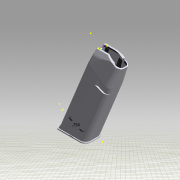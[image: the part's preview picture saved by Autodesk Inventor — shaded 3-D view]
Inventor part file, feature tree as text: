
AUTODESK INVENTOR PART (.ipt)
format: ipt  version: 2018 (Build 220112000, 112)  size: 5,122,560 bytes
history: native  units: mm (DEFAULTED — no unit token found)
features: sketch x117, extrude x106, projected_geometry x105, mirror x43, plane x19, fillet x14, direct_edit x5, other x5, chamfer x4, loft x2, revolve x2, sweep x1
ambient origin geometry x8: Origin, YZ Plane, XZ Plane, XY Plane, X Axis, Y Axis, Z Axis, Center Point
bodies: Solid2 (feature_tree), Solid1 (feature_tree)
feature tree (423):
  direct_edit  "Direct Edit1"
  direct_edit  "Direct Edit2"
  direct_edit  "Direct Edit3"
  extrude  "Extrusion1"  Depth=10.0mm
  extrude  "Extrusion2"  Depth=0.4064mm
  extrude  "Extrusion3"  Depth=25.4mm TaperAngle=0.0deg
  extrude  "Extrusion4"  Depth=0.4064mm TaperAngle=0.0deg
  fillet  "Fillet1"  Radius=0.254mm
  extrude  "Extrusion5"  Depth=1.905mm
  extrude  "Extrusion7"  Depth=50.8mm TaperAngle=0.0deg
  extrude  "Extrusion8"  Depth=2.54mm TaperAngle=0.0deg
  extrude  "Extrusion9"  Depth=2.54mm TaperAngle=0.0deg
  extrude  "Extrusion10"  [1 undecoded]
  extrude  "Extrusion11"  Depth=4.0mm TaperAngle=0.0deg
  extrude  "Extrusion12"  Depth=4.0mm TaperAngle=0.0deg
  extrude  "Extrusion13"  Depth=8.0mm TaperAngle=0.0deg
  direct_edit  "Direct Edit4"
  plane  "Work Plane1"
  plane  "Work Plane2"
  extrude  "Extrusion20"  Depth=2.0mm TaperAngle=0.0deg
  extrude  "Extrusion21"  Depth=2.0mm TaperAngle=0.0deg
  mirror  "Mirror2"
  extrude  "Extrusion22"  [1 undecoded]
  extrude  "Extrusion23"  Depth=2.0mm TaperAngle=0.0deg
  extrude  "Extrusion24"  Depth=2.0mm TaperAngle=0.0deg
  mirror  "Mirror3"
  extrude  "Extrusion25"  Depth=2.0mm TaperAngle=0.0deg
  extrude  "Extrusion26"  Depth=2.0mm TaperAngle=0.0deg
  extrude  "Extrusion27"  Depth=2.0mm TaperAngle=0.0deg
  extrude  "Extrusion28"  Depth=2.0mm TaperAngle=0.0deg
  extrude  "Extrusion29"  TaperAngle=0.0deg  [1 undecoded]
  extrude  "Extrusion30"  Depth=0.5mm TaperAngle=0.0deg
  plane  "Work Plane3"
  extrude  "Extrusion31"  Depth=0.142mm TaperAngle=0.0deg
  extrude  "Extrusion32"  Depth=0.142mm TaperAngle=0.0deg
  extrude  "Extrusion33"  Depth=0.142mm TaperAngle=0.0deg
  mirror  "Mirror4"
  extrude  "Extrusion34"  Depth=0.142mm TaperAngle=0.0deg
  extrude  "Extrusion36"  Depth=4.3053mm
  extrude  "Extrusion37"  Depth=1.0mm TaperAngle=0.0deg
  extrude  "Extrusion38"  TaperAngle=0.0deg  [1 undecoded]
  extrude  "Extrusion39"  Depth=0.05mm TaperAngle=0.0deg
  mirror  "Mirror5"
  extrude  "Extrusion41"  Depth=25.4mm TaperAngle=0.0deg
  extrude  "Extrusion42"  Depth=25.4mm TaperAngle=0.0deg
  extrude  "Extrusion43"  Depth=304.8mm TaperAngle=0.0deg
  mirror  "Mirror6"
  mirror  "Mirror7"
  extrude  "Extrusion44"  Depth=2.54mm
  loft  "Loft1"
  mirror  "Mirror8"
  sketch  "Sketch62"  dims[d190=12.7mm d191=0.0mm d237=90.0deg]
  sketch  "Sketch63"  dims[d238=0.2032mm d240=2.54mm]
  sketch  "Sketch64"  dims[d241=0.0mm d242=0.0mm d245=1.27mm d246=0.0mm]
  plane  "Work Plane5"
  extrude  "Extrusion45"  Depth=12.7mm TaperAngle=0.0deg
  extrude  "Extrusion46"  TaperAngle=90.0deg  [1 undecoded]
  extrude  "Extrusion47"  Depth=2.54mm
  extrude  "Extrusion48"  Depth=1.27mm TaperAngle=0.0deg
  extrude  "Extrusion49"  Depth=0.381mm
  extrude  "Extrusion50"  Depth=0.1905mm
  extrude  "Extrusion51"  Depth=0.254mm TaperAngle=0.0deg
  extrude  "Extrusion52"  Depth=0.254mm TaperAngle=0.0deg
  extrude  "Extrusion54"  Depth=0.254mm
  extrude  "Extrusion55"  Depth=0.35mm TaperAngle=0.0deg
  extrude  "Extrusion56"  TaperAngle=90.0deg  [1 undecoded]
  mirror  "Mirror9"
  extrude  "Extrusion57"  Depth=2.413mm TaperAngle=0.0deg
  plane  "Work Plane6"
  loft  "Loft2"
  mirror  "Mirror10"
  mirror  "Mirror11"
  extrude  "Extrusion58"  Depth=2.794mm
  direct_edit  "Direct Edit6"
  extrude  "Extrusion60"  Depth=381.0mm
  mirror  "Mirror14"
  plane  "Work Plane7"
  extrude  "Extrusion61"  Depth=762.0mm
  mirror  "Mirror15"
  plane  "Work Plane8"
  extrude  "Extrusion62"  Depth=0.635mm
  mirror  "Mirror16"
  extrude  "Extrusion63"  Depth=96.52mm TaperAngle=0.0deg
  fillet  "Fillet3"  Radius=254.0mm
  extrude  "Extrusion65"  Depth=0.635mm
  mirror  "Mirror18"
  plane  "Work Plane9"
  extrude  "Extrusion66"  Depth=83.82mm TaperAngle=0.0deg
  extrude  "Extrusion67"  TaperAngle=90.0deg  [1 undecoded]
  mirror  "Mirror19"
  plane  "Work Plane16"
  plane  "Work Plane15"
  fillet  "Fillet20"  Radius=0.762mm
  sweep  "Sweep3"
  plane  "Work Plane17"
  extrude  "Extrusion81"  Depth=25.4mm TaperAngle=0.0deg
  extrude  "Extrusion82"  Depth=25.4mm TaperAngle=0.0deg
  mirror  "Mirror30"
  sketch  "Sketch133"  dims[d363=25.4mm d364=0.0mm d410=1.016mm d411=0.0mm]
  extrude  "Extrusion84"  Depth=0.381mm TaperAngle=0.0deg
  mirror  "Mirror32"
  extrude  "Extrusion85"  Depth=1.016mm TaperAngle=0.0deg
  extrude  "Extrusion86"  Depth=1.016mm TaperAngle=0.0deg
  extrude  "Extrusion87"  Depth=1.778mm TaperAngle=0.0deg
  fillet  "Fillet21"  Radius=1.27mm
  mirror  "Mirror33"
  mirror  "Mirror34"
  extrude  "Extrusion88"  Depth=88.9mm TaperAngle=0.0deg
  mirror  "Mirror35"
  extrude  "Extrusion89"  Depth=1.27mm TaperAngle=0.0deg
  chamfer  "Chamfer1"  Distance=3.048mm
  plane  "Work Plane18"
  extrude  "Extrusion90"  Depth=2.54mm TaperAngle=0.0deg
  extrude  "Extrusion91"  Depth=19.15mm
  mirror  "Mirror36"
  plane  "Work Plane19"
  extrude  "Extrusion92"  Depth=2.54mm TaperAngle=0.0deg
  chamfer  "Chamfer2"  Distance=2.54mm
  chamfer  "Chamfer3"  Distance=2.54mm
  extrude  "Extrusion93"  Depth=2.54mm TaperAngle=0.0deg
  mirror  "Mirror37"
  fillet  "Fillet23"  Radius=0.5588mm
  chamfer  "Chamfer4"  Distance=25.4mm
  fillet  "Fillet24"  Radius=25.4mm
  fillet  "Fillet25"  Radius=25.4mm
  fillet  "Fillet26"  Radius=25.4mm
  mirror  "Mirror39"
  extrude  "Extrusion94"  Depth=2.032mm TaperAngle=0.0deg
  mirror  "Mirror40"
  fillet  "Fillet27"  Radius=1.524mm
  extrude  "Extrusion95"  Depth=0.381mm TaperAngle=0.0deg
  mirror  "Mirror41"
  extrude  "Extrusion96"  Depth=0.5588mm
  mirror  "Mirror42"
  plane  "Work Plane20"
  plane  "Work Plane21"
  plane  "Work Plane22"
  extrude  "Extrusion97"  Depth=0.254mm
  mirror  "Mirror43"
  extrude  "Extrusion98"  [1 undecoded]
  extrude  "Extrusion99"  [1 undecoded]
  extrude  "Extrusion100"  [1 undecoded]
  extrude  "Extrusion101"  [1 undecoded]
  extrude  "Extrusion102"  [1 undecoded]
  mirror  "Mirror44"
  extrude  "Extrusion104"  [1 undecoded]
  extrude  "Extrusion105"  [1 undecoded]
  mirror  "Mirror46"
  extrude  "Extrusion106"  [1 undecoded]
  mirror  "Mirror47"
  plane  "Work Plane23"
  extrude  "Extrusion127"  [1 undecoded]
  extrude  "Extrusion128"  [1 undecoded]
  extrude  "Extrusion129"  [1 undecoded]
  extrude  "Extrusion130"  [1 undecoded]
  mirror  "Mirror50"
  sketch  "Sketch192"
  extrude  "Extrusion132"  [1 undecoded]
  extrude  "Extrusion133"  [1 undecoded]
  mirror  "Mirror52"
  extrude  "Extrusion134"  [1 undecoded]
  mirror  "Mirror53"
  extrude  "Extrusion135"  [1 undecoded]
  extrude  "Extrusion136"  [1 undecoded]
  extrude  "Extrusion137"  [1 undecoded]
  mirror  "Mirror54"
  extrude  "Extrusion138"  [1 undecoded]
  extrude  "Extrusion139"  [1 undecoded]
  extrude  "Extrusion140"  [1 undecoded]
  extrude  "Extrusion141"  [1 undecoded]
  sketch  "Sketch202"
  mirror  "Mirror55"
  sketch  "Sketch203"
  sketch  "Sketch204"
  sketch  "Sketch205"
  extrude  "Extrusion143"  [1 undecoded]
  mirror  "Mirror56"
  extrude  "Extrusion144"  [1 undecoded]
  extrude  "Extrusion146"  [1 undecoded]
  mirror  "Mirror58"
  extrude  "Extrusion147"  [1 undecoded]
  mirror  "Mirror59"
  fillet  "Fillet38"  [1 undecoded]
  extrude  "Extrusion148"  [1 undecoded]
  extrude  "Extrusion150"  [1 undecoded]
  mirror  "Mirror60"
  plane  "Work Plane24"
  sketch  "Sketch216"
  extrude  "Extrusion153"  [1 undecoded]
  mirror  "Mirror61"
  sketch  "Sketch217"
  extrude  "Extrusion154"  [1 undecoded]
  extrude  "Extrusion155"  [1 undecoded]
  sketch  "Sketch224"
  extrude  "Extrusion156"  [1 undecoded]
  fillet  "Fillet39"  [1 undecoded]
  fillet  "Fillet40"  [1 undecoded]
  sketch  "Sketch226"
  sketch  "Sketch227"
  sketch  "Sketch228"
  extrude  "Extrusion158"  [1 undecoded]
  extrude  "Extrusion159"  [1 undecoded]
  mirror  "Mirror64"
  fillet  "Fillet44"  [1 undecoded]
  extrude  "Extrusion160"  [1 undecoded]
  fillet  "Fillet45"  [1 undecoded]
  mirror  "Mirror65"
  mirror  "Mirror66"
  sketch  "Sketch1"  dims[d0=9.75mm d1=10.0mm d2=10.0mm d3=10.0mm d4=10.0mm d5=10.15mm]
  projected_geometry  "Projected Loop1"
  projected_geometry  "Projected Loop2"
  projected_geometry  "Projected Loop3"
  sketch  "Sketch4"  dims[d6=10.0mm d7=10.3mm d8=10.0mm d9=0.4064mm]
  projected_geometry  "Projected Loop4"
  projected_geometry  "Projected Loop5"
  sketch  "Sketch5"  dims[d10=25.4mm d11=0.0mm d12=25.4mm d13=0.0mm]
  projected_geometry  "Projected Loop6"
  sketch  "Sketch6"  dims[d14=2.54mm d15=0.0mm d16=0.4064mm d17=0.0mm d18=0.254mm]
  projected_geometry  "Projected Loop7"
  sketch  "Sketch9"  dims[d19=50.8mm d20=0.0mm d21=1.905mm]
  sketch  "Sketch10"  dims[d24=50.8mm d25=0.0mm d26=50.8mm d27=0.0mm]
  sketch  "Sketch11"  dims[d28=2.54mm d29=0.0mm d30=2.54mm d31=0.0mm]
  projected_geometry  "Projected Loop8"
  sketch  "Sketch12"  dims[d32=2.54mm d33=0.0mm d34=2.54mm d35=0.0mm]
  projected_geometry  "Projected Loop9"
  sketch  "Sketch13"  dims[d36=1.0mm d37=0.0mm d39=-3.665191mm]
  projected_geometry  "Projected Loop10"
  sketch  "Sketch14"  dims[d57=1.5mm d58=0.0mm d59=4.0mm d60=0.0mm]
  sketch  "Sketch15"  dims[d61=4.0mm d62=0.0mm d63=4.0mm d64=0.0mm]
  projected_geometry  "Projected Loop11"
  sketch  "Sketch17"  dims[d65=8.0mm d66=0.0mm d67=8.0mm d68=0.0mm]
  sketch  "Sketch30"  dims[d69=2.0mm d70=0.0mm d71=2.0mm d72=0.0mm]
  sketch  "Sketch31"  dims[d73=2.0mm d74=0.0mm d75=2.0mm d76=0.0mm]
  projected_geometry  "Projected Loop21"
  projected_geometry  "Projected Loop22"
  sketch  "Sketch32"  dims[d77=2.0mm d78=0.0mm d79=-8.11mm]
  sketch  "Sketch33"  dims[d80=2.0mm d81=0.0mm d82=2.0mm d83=0.0mm]
  projected_geometry  "Projected Loop23"
  sketch  "Sketch34"  dims[d84=2.0mm d85=0.0mm d86=2.0mm d87=0.0mm]
  projected_geometry  "Projected Loop24"
  sketch  "Sketch35"  dims[d90=1.0mm d91=0.0mm d92=2.0mm d93=0.0mm]
  projected_geometry  "Projected Loop25"
  sketch  "Sketch37"  dims[d94=2.0mm d95=0.0mm d96=2.0mm d97=0.0mm]
  projected_geometry  "Projected Loop27"
  sketch  "Sketch39"  dims[d100=2.0mm d101=0.0mm d102=2.0mm d103=0.0mm]
  sketch  "Sketch40"  dims[d104=2.0mm d105=0.0mm d106=2.0mm d107=0.0mm]
  projected_geometry  "Projected Loop29"
  sketch  "Sketch41"  dims[d108=0.0mm d109=90.0deg d110=0.0mm d111=90.0deg]
  sketch  "Sketch42"  dims[d112=90.0deg d113=0.127mm d114=0.5mm d115=0.0mm]
  projected_geometry  "Projected Loop30"
  sketch  "Sketch44"  dims[d116=0.5mm d117=0.0mm d118=0.142mm d119=0.0mm]
  sketch  "Sketch45"  dims[d120=0.142mm d121=0.0mm d122=0.142mm d123=0.0mm]
  projected_geometry  "Projected Loop31"
  sketch  "Sketch46"  dims[d124=0.142mm d125=0.0mm d126=0.142mm d127=0.0mm]
  sketch  "Sketch47"  dims[d128=0.142mm d129=0.0mm d132=0.142mm d133=0.0mm]
  projected_geometry  "Projected Loop32"
  sketch  "Sketch49"  dims[d134=0.142mm d135=0.0mm d136=4.3053mm]
  projected_geometry  "Projected Loop34"
  sketch  "Sketch50"  dims[d137=2.0mm d138=0.0mm d139=1.0mm d140=0.0mm]
  projected_geometry  "Projected Loop35"
  sketch  "Sketch51"  dims[d141=-2.5mm d142=0.0mm d143=90.0deg]
  projected_geometry  "Projected Loop36"
  sketch  "Sketch52"  dims[d144=0.0mm d145=90.0deg d146=0.05mm d147=0.0mm]
  projected_geometry  "Projected Loop37"
  sketch  "Sketch53"  dims[d153=-0.191986mm d166=25.4mm d167=0.0mm]
  projected_geometry  "Projected Loop38"
  sketch  "Sketch54"  dims[d168=90.0deg d169=25.4mm d170=0.0mm]
  projected_geometry  "Projected Loop39"
  sketch  "Sketch55"  dims[d171=90.0deg d173=304.8mm d174=0.0mm]
  projected_geometry  "Projected Loop40"
  sketch  "Sketch58"  dims[d175=304.8mm d176=0.0mm d177=2.54mm]
  projected_geometry  "Projected Loop42"
  sketch  "Sketch60"  dims[d184=0.254mm d185=304.8mm d186=0.0mm]
  sketch  "Sketch61"  dims[d187=90.0deg d188=12.7mm d189=0.0mm]
  projected_geometry  "Projected Loop44"
  projected_geometry  "Projected Loop45"
  projected_geometry  "Projected Loop46"
  projected_geometry  "Projected Loop47"
  projected_geometry  "Projected Loop48"
  plane  "Work Plane4"
  sketch  "Sketch65"  dims[d247=50.8mm d248=0.0mm d251=0.381mm]
  projected_geometry  "Projected Loop49"
  sketch  "Sketch67"  dims[d252=5.08mm d253=0.1905mm]
  projected_geometry  "Projected Loop50"
  sketch  "Sketch68"  dims[d254=0.762mm d255=0.254mm d256=0.0mm]
  projected_geometry  "Projected Loop51"
  sketch  "Sketch69"  dims[d257=6.35mm d258=0.0mm d259=0.254mm d260=0.0mm]
  projected_geometry  "Projected Loop52"
  sketch  "Sketch70"  dims[d261=0.254mm d262=0.0mm d263=0.254mm]
  projected_geometry  "Projected Loop53"
  sketch  "Sketch71"  dims[d265=3.81mm d266=0.0mm d267=0.35mm d268=0.0mm]
  sketch  "Sketch72"  dims[d269=0.23mm d270=3.175mm d271=45.0deg d274=90.0deg]
  projected_geometry  "Projected Loop54"
  sketch  "Sketch73"  dims[d275=2.413mm d276=0.0mm d277=2.413mm d278=0.0mm]
  sketch  "Sketch74"  dims[d280=-0.0635mm d281=25.4mm d282=0.0mm]
  projected_geometry  "Projected Loop55"
  other  "Edges1"
  other  "Edges2"
  sketch  "Sketch78"  dims[d283=12.7mm d284=3.175mm d285=0.198968mm d286=2.794mm d287=3.175mm d288=0.872665mm]
  projected_geometry  "Projected Loop57"
  sketch  "Sketch86"  dims[d289=25.4mm d290=0.0mm d291=381.0mm]
  projected_geometry  "Projected Loop62"
  sketch  "Sketch87"  dims[d292=12.7mm d293=3.175mm d294=0.198968mm d295=762.0mm]
  projected_geometry  "Projected Loop63"
  projected_geometry  "Projected Loop64"
  projected_geometry  "Projected Loop65"
  projected_geometry  "Projected Loop66"
  sketch  "Sketch90"  dims[d296=1.27mm d297=0.635mm]
  projected_geometry  "Projected Loop70"
  sketch  "Sketch91"  dims[d298=0.5588mm d299=96.52mm d300=0.0mm d301=254.0mm]
  projected_geometry  "Projected Loop71"
  sketch  "Sketch93"  dims[d302=25.4mm d303=0.0mm d304=0.635mm]
  sketch  "Sketch97"  dims[d305=0.635mm d306=83.82mm d307=0.0mm]
  projected_geometry  "Projected Loop75"
  sketch  "Sketch98"  dims[d308=90.0deg d309=90.0deg d310=-0.8128mm d311=0.762mm]
  projected_geometry  "Projected Loop76"
  sketch  "Sketch126"  dims[d312=1.397mm d313=0.0mm d317=25.4mm d318=0.0mm]
  sketch  "Sketch127"  dims[d319=25.4mm d320=0.0mm d321=25.4mm d322=0.0mm]
  projected_geometry  "Projected Loop104"
  sketch  "Sketch130"  dims[d323=25.4mm d324=0.0mm d325=25.4mm d326=0.0mm]
  projected_geometry  "Projected Loop106"
  projected_geometry  "Projected Loop107"
  sketch  "Sketch131"  dims[d359=0.381mm d360=0.0mm d361=0.381mm d362=0.0mm]
  projected_geometry  "Projected Loop109"
  sketch  "Sketch136"  dims[d412=1.016mm d413=0.0mm d414=1.016mm d415=0.0mm]
  projected_geometry  "Projected Loop110"
  projected_geometry  "Projected Loop111"
  sketch  "Sketch137"  dims[d416=0.508mm d417=0.0mm d420=1.778mm d421=0.0mm d422=1.27mm d423=0.0mm]
  projected_geometry  "Projected Loop112"
  sketch  "Sketch138"  dims[d424=1.27mm d425=0.0mm d426=88.9mm d427=0.0mm]
  projected_geometry  "Projected Loop113"
  sketch  "Sketch139"  dims[d428=1.27mm d429=0.0mm d430=1.27mm d431=0.0mm d432=3.048mm d433=0.0mm]
  projected_geometry  "Projected Loop114"
  sketch  "Sketch140"  dims[d434=3.048mm d435=0.0mm d438=2.54mm d439=0.0mm]
  projected_geometry  "Projected Loop115"
  sketch  "Sketch143"  dims[d440=2.54mm d441=0.0mm d442=19.15mm]
  sketch  "Sketch144"  dims[d443=1.524mm d444=0.0mm d450=2.54mm d451=0.0mm d453=2.54mm d454=0.0mm]
  sketch  "Sketch146"  dims[d462=4.572mm d463=2.54mm d464=0.0mm]
  projected_geometry  "Projected Loop116"
  sketch  "Sketch147"  dims[d466=90.0deg d467=2.54mm d468=0.0mm d469=0.5588mm d470=25.4mm d471=0.0mm d474=25.4mm d475=0.0mm d481=25.4mm d482=0.0mm d483=25.4mm d484=0.0mm]
  sketch  "Sketch148"  dims[d485=25.4mm d486=0.0mm d487=2.032mm d488=0.0mm d489=1.524mm]
  projected_geometry  "Projected Loop117"
  sketch  "Sketch149"  dims[d490=5.08mm d495=0.381mm d496=0.0mm]
  projected_geometry  "Projected Loop118"
  sketch  "Sketch150"  dims[d497=0.381mm d498=0.0mm d501=0.5588mm]
  sketch  "Sketch153"  dims[d502=25.4mm d503=0.0mm d504=0.254mm]
  projected_geometry  "Projected Loop120"
  projected_geometry  "Projected Loop121"
  projected_geometry  "Projected Loop122"
  sketch  "Sketch154"
  sketch  "Sketch155"
  projected_geometry  "Projected Loop123"
  projected_geometry  "Projected Loop124"
  sketch  "Sketch156"
  projected_geometry  "Projected Loop125"
  sketch  "Sketch157"
  projected_geometry  "Projected Loop126"
  sketch  "Sketch158"
  projected_geometry  "Projected Loop127"
  sketch  "Sketch163"
  projected_geometry  "Projected Loop132"
  sketch  "Sketch164"
  sketch  "Sketch165"
  projected_geometry  "Projected Loop133"
  projected_geometry  "Projected Loop134"
  projected_geometry  "Projected Loop147"
  sketch  "Sketch189"
  projected_geometry  "Projected Loop149"
  sketch  "Sketch190"
  projected_geometry  "Projected Loop150"
  sketch  "Sketch191"
  projected_geometry  "Projected Loop151"
  sketch  "Sketch193"
  projected_geometry  "Projected Loop153"
  sketch  "Sketch194"
  projected_geometry  "Projected Loop154"
  sketch  "Sketch195"
  projected_geometry  "Projected Loop155"
  sketch  "Sketch196"
  projected_geometry  "Projected Loop156"
  projected_geometry  "Projected Loop157"
  sketch  "Sketch197"
  projected_geometry  "Projected Loop158"
  sketch  "Sketch198"
  projected_geometry  "Projected Loop159"
  sketch  "Sketch199"
  projected_geometry  "Projected Loop160"
  projected_geometry  "Projected Loop161"
  sketch  "Sketch200"
  projected_geometry  "Projected Loop162"
  projected_geometry  "Projected Loop163"
  projected_geometry  "Projected Loop164"
  sketch  "Sketch201"
  projected_geometry  "Projected Loop165"
  projected_geometry  "Projected Loop166"
  projected_geometry  "Projected Loop167"
  projected_geometry  "Projected Loop168"
  projected_geometry  "Projected Loop169"
  sketch  "Sketch206"
  projected_geometry  "Projected Loop170"
  sketch  "Sketch208"
  projected_geometry  "Projected Loop172"
  sketch  "Sketch209"
  projected_geometry  "Projected Loop173"
  sketch  "Sketch210"
  sketch  "Sketch213"
  projected_geometry  "Projected Loop175"
  sketch  "Sketch219"
  projected_geometry  "Projected Loop181"
  projected_geometry  "Projected Loop182"
  projected_geometry  "Projected Loop183"
  sketch  "Sketch222"
  projected_geometry  "Projected Loop186"
  sketch  "Sketch225"
  sketch  "Sketch230"
  sketch  "Sketch231"
  projected_geometry  "Projected Loop191"
  sketch  "Sketch232"
  other  "Scale1"
  other  "Scale2"
  other  "Scale3"
  revolve  "Rotate1"  [1 undecoded]
  revolve  "Rotate5"  [1 undecoded]
note: 49 required parameter values undecoded (feature->parameter linkage not recoverable at this tier; creation-order binding heuristic only, values carry confidence <= 0.55)
